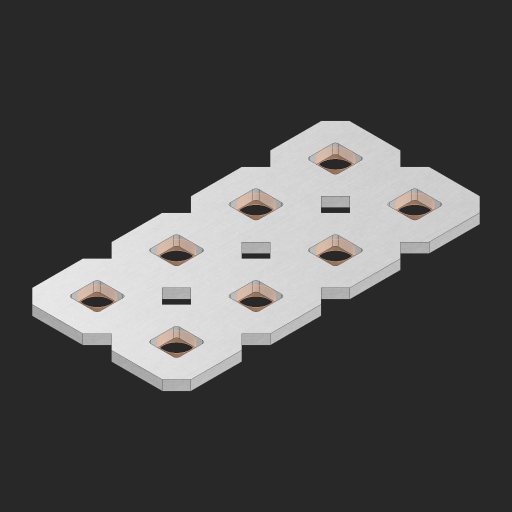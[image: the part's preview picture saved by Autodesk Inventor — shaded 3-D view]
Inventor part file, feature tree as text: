
AUTODESK INVENTOR PART (.ipt)
format: ipt  version: 2023 (Build 270158000, 158)  size: 382,976 bytes
history: native  units: in
note: dims shown in document units (in); Inventor stores cm internally (conversion verified against a paired STEP export)
features: other x9, extrude x7, sketch x2, pattern_linear x1
ambient origin geometry x8: Origin, YZ Plane, XZ Plane, XY Plane, X Axis, Y Axis, Z Axis, Center Point
bodies: Solid1 (feature_tree), Body (feature_tree)
feature tree (19):
  pattern_linear  "Rectangular Pattern1"  Spacing1=0.09in  [1 undecoded]
  sketch  "Sketch1"  dims[d1=0.5in]
  sketch  "Sketch2"  dims[d2=0.182in d3=0.09in d4=0.09in d5=0.09in d6=0.09in d7=0.09in d8=0.09in d9=0.09in d10=0.09in d11=0.02in d13=0.0in d14=0.172in d15=0.0625in d16=0.0in d19=0.5in d22=0.5in]
  other  "Srf1"
  other  "Srf126"
  other  "Srf127"
  other  "Srf128"
  other  "Srf268"
  other  "Srf269"
  other  "Srf270"
  other  "Srf271"
  other  "Circle"
  extrude  "ExtrusionSrf126"  Depth=0.09in
  extrude  "ExtrusionSrf127"  Depth=0.09in
  extrude  "ExtrusionSrf128"  Depth=0.09in
  extrude  "ExtrusionSrf268"  Depth=0.09in
  extrude  "ExtrusionSrf269"  Depth=0.09in
  extrude  "ExtrusionSrf270"  Depth=0.09in
  extrude  "ExtrusionSrf271"  Depth=0.09in
note: 1 required parameter value undecoded (feature->parameter linkage not recoverable at this tier; creation-order binding heuristic only, values carry confidence <= 0.55)
